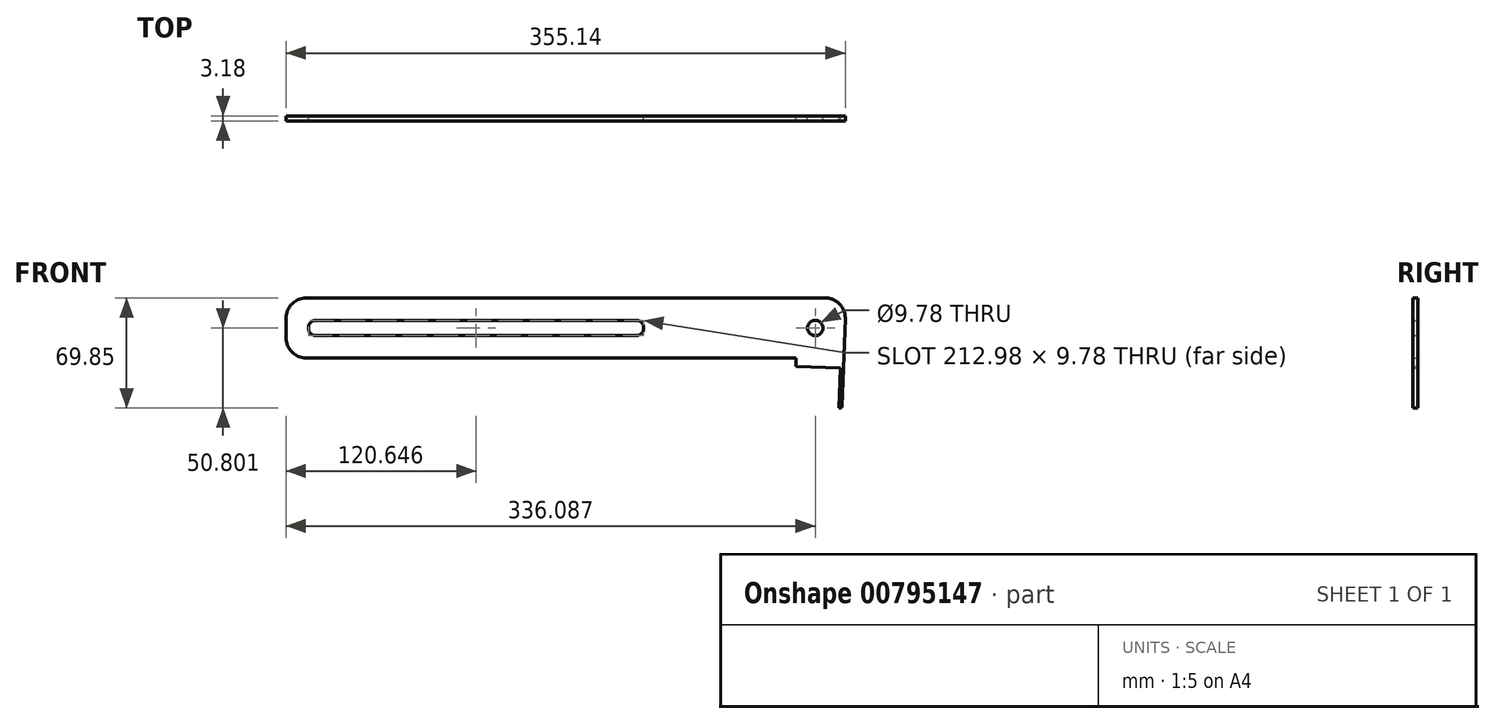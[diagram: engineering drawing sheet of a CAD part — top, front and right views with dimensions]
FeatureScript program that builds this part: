
annotation { "Feature Type Name" : "Feature", "Feature Type Description" : "" }
export const myFeature = defineFeature(function(context is Context, id is Id, definition is map)
    precondition{}
    {
        {
            var Q0;
            Q0=qCreatedBy(makeId("Front.planeOp"),FACE);
            var sketch = newSketch(context, id + "F0", { "sketchPlane" : qUnion([Q0])});
            skLineSegment(sketch, "E0", {"start": v(-193.62, -52.78) * mm, "end": v(136.12, -52.78) * mm});
            skLineSegment(sketch, "E1", {"start": v(117.53, -90.88) * mm, "end": v(-193.62, -90.88) * mm});
            skLineSegment(sketch, "E2", {"start": v(-206.32, -78.18) * mm, "end": v(-206.32, -65.48) * mm});
            skPoint(sketch, "E3.end.orphan", {"position": v(146.84, -76.53) * mm});
            skLineSegment(sketch, "E4", {"start": v(148.82, -65.92) * mm, "end": v(146.88, -121.35) * mm});
            skLineSegment(sketch, "E5", {"start": v(145.56, -122.63) * mm, "end": v(144.8, -122.63) * mm});
            skLineSegment(sketch, "E6", {"start": v(121.44, -103.8) * mm, "end": v(121.44, -103.8) * mm});
            skPoint(sketch, "E7.visualSharp", {"position": v(146.84, -122.63) * mm});
            skArc(sketch, "E7.filletArc", {"start": v(145.56, -122.63) * mm, "mid": v(146.48, -122.26) * mm, "end": v(146.88, -121.35) * mm});
            skLineSegment(sketch, "E8", {"start": v(144.8, -122.63) * mm, "end": v(145.7, -97.23) * mm});
            skPoint(sketch, "E9.end.orphan", {"position": v(144.5, -97.23) * mm});
            skLineSegment(sketch, "E10", {"start": v(145.7, -97.23) * mm, "end": v(117.53, -96.25) * mm});
            skLineSegment(sketch, "E11", {"start": v(117.53, -96.25) * mm, "end": v(117.53, -90.88) * mm});
            skPoint(sketch, "E12.visualSharp", {"position": v(149.28, -52.78) * mm});
            skArc(sketch, "E12.filletArc", {"start": v(148.82, -65.92) * mm, "mid": v(145.26, -56.66) * mm, "end": v(136.12, -52.78) * mm});
            skPoint(sketch, "E13.visualSharp", {"position": v(-206.32, -90.88) * mm});
            skArc(sketch, "E13.filletArc", {"start": v(-206.32, -78.18) * mm, "mid": v(-202.6, -87.16) * mm, "end": v(-193.62, -90.88) * mm});
            skPoint(sketch, "E14.visualSharp", {"position": v(-206.32, -52.78) * mm});
            skArc(sketch, "E14.filletArc", {"start": v(-193.62, -52.78) * mm, "mid": v(-202.6, -56.5) * mm, "end": v(-206.32, -65.48) * mm});
            skArc(sketch, "E15", {"start": v(-187.27, -66.94) * mm, "mid": v(-192.16, -71.83) * mm, "end": v(-187.27, -76.72) * mm});
            skPoint(sketch, "E15.centerSnap0", {"position": v(-206.32, -71.83) * mm});
            skArc(sketch, "E16", {"start": v(15.93, -76.72) * mm, "mid": v(20.82, -71.83) * mm, "end": v(15.93, -66.94) * mm});
            skLineSegment(sketch, "E17", {"start": v(15.93, -76.72) * mm, "end": v(-187.27, -76.72) * mm});
            skLineSegment(sketch, "E18", {"start": v(-187.27, -66.94) * mm, "end": v(15.93, -66.94) * mm});
            skCircle(sketch, "E19", {"center": v(129.77, -71.83) * mm, "radius": 4.89 * mm});
            skSolve(sketch);
        }
        {
            var Q0;
            Q0=makeQuery(id+"F0.imprint","IMPRINT",FACE,{"disambiguationData":[TD([[makeQuery(id+"F0.imprint","IMPRINT",EDGE,{"derivedFrom":sQuery(id+"F0.wireOp",EDGE,"E0")}),-1.0]])]});
            extrude(context, id + "F1", {"entities" : qUnion([Q0]), "depth" : 3.17 * mm, "offsetDistance" : 25.4 * mm});
        }
    });
